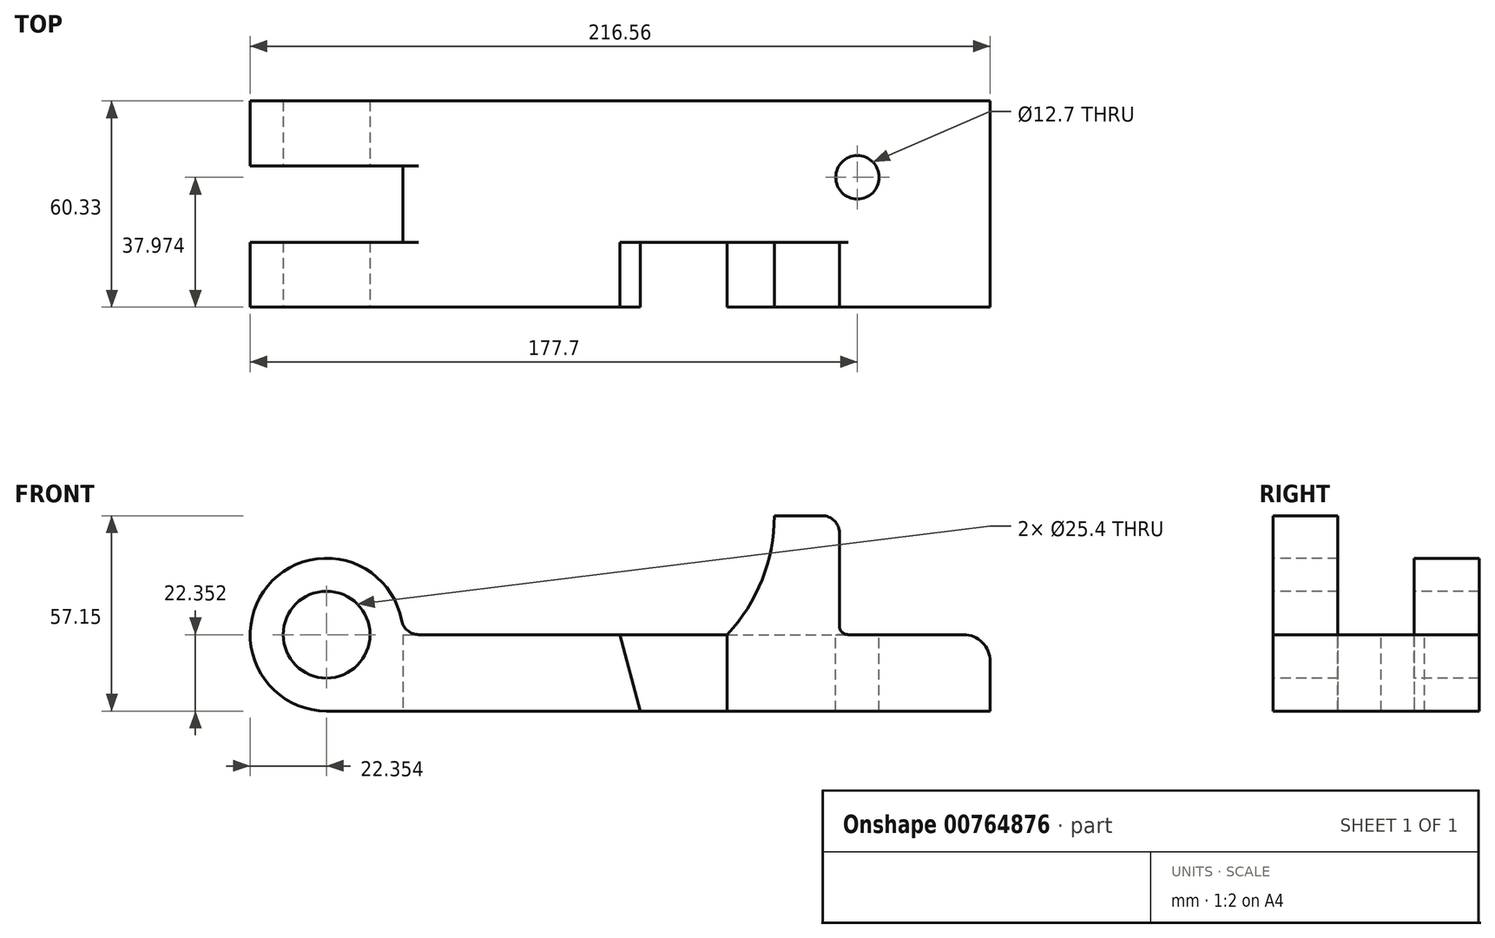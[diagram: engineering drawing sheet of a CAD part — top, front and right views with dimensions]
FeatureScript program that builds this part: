
annotation { "Feature Type Name" : "Feature", "Feature Type Description" : "" }
export const myFeature = defineFeature(function(context is Context, id is Id, definition is map)
    precondition{}
    {
        {
            var Q0;
            Q0=qCreatedBy(makeId("Front.planeOp"),FACE);
            var sketch = newSketch(context, id + "F0", { "sketchPlane" : qUnion([Q0])});
            skLineSegment(sketch, "E0", {"start": v(-51.89, 0) * mm, "end": v(142.32, 0) * mm});
            skLineSegment(sketch, "E1", {"start": v(142.32, 0) * mm, "end": v(142.32, 22.35) * mm});
            skLineSegment(sketch, "E2", {"start": v(-51.89, 0) * mm, "end": v(-51.89, 22.35) * mm});
            skCircle(sketch, "E3", {"center": v(-51.89, 22.35) * mm, "radius": 22.35 * mm});
            skCircle(sketch, "E4", {"center": v(-51.89, 22.35) * mm, "radius": 12.7 * mm});
            skLineSegment(sketch, "E5", {"start": v(-51.89, 22.35) * mm, "end": v(142.32, 22.35) * mm});
            skSolve(sketch);
        }
        {
            var Q0;
            {var subQ0=sQuery(id+"F0.wireOp",EDGE,"E0");Q0=makeQuery(id+"F0.imprint","IMPRINT",FACE,{"disambiguationData":[TD([[makeQuery(id+"F0.imprint","IMPRINT",EDGE,{"derivedFrom":subQ0}),1.0]])]});}
            var Q1;
            {var subQ1=sQuery(id+"F0.wireOp",EDGE,"E2");var subQ3=sQuery(id+"F0.wireOp",EDGE,"E4");var subQ4=makeQuery(id+"F0.imprint","INTERSECT",VERTEX,{"derivedFrom":[subQ1,subQ3]});Q1=makeQuery(id+"F0.imprint","IMPRINT",FACE,{"disambiguationData":[TD([[makeQuery(id+"F0.imprint","IMPRINT",EDGE,{"disambiguationData":[TD([[subQ4,1.0]])],"derivedFrom":subQ3}),-1.0]])]});}
            var Q2;
            {var subQ1=sQuery(id+"F0.wireOp",EDGE,"E2");var subQ3=sQuery(id+"F0.wireOp",EDGE,"E4");var subQ4=makeQuery(id+"F0.imprint","INTERSECT",VERTEX,{"derivedFrom":[subQ1,subQ3]});Q2=makeQuery(id+"F0.imprint","IMPRINT",FACE,{"disambiguationData":[TD([[makeQuery(id+"F0.imprint","IMPRINT",EDGE,{"disambiguationData":[TD([[subQ4,-1.0]])],"derivedFrom":subQ3}),-1.0]])]});}
            extrude(context, id + "F1", {"entities" : qUnion([Q0, Q1, Q2]), "oppositeDirection" : true, "depth" : 41.33 * mm, "offsetDistance" : 25.4 * mm});
        }
        {
            var Q0;
            Q0=makeQuery(id+"F1.opExtrude","CAP_FACE",FACE,{"disambiguationData":[OSD([sQuery(id+"F0.wireOp",EDGE,"E0"),sQuery(id+"F0.wireOp",EDGE,"E1"),sQuery(id+"F0.wireOp",EDGE,"E3"),sQuery(id+"F0.wireOp",EDGE,"E4"),sQuery(id+"F0.wireOp",EDGE,"E5")])],"isStart":true});
            var sketch = newSketch(context, id + "F2", { "sketchPlane" : qUnion([Q0])});
            skCircle(sketch, "E6", {"center": v(-51.89, 22.35) * mm, "radius": 12.7 * mm});
            skCircle(sketch, "E7", {"center": v(-51.89, 22.35) * mm, "radius": 22.35 * mm});
            skLineSegment(sketch, "E8", {"start": v(-29.53, 22.35) * mm, "end": v(142.32, 22.35) * mm});
            skLineSegment(sketch, "E9", {"start": v(142.32, 22.35) * mm, "end": v(142.32, 0) * mm});
            skLineSegment(sketch, "E10", {"start": v(142.32, 0) * mm, "end": v(-51.89, 0) * mm});
            skLineSegment(sketch, "E11", {"start": v(33.97, 22.35) * mm, "end": v(39.96, 0) * mm});
            skLineSegment(sketch, "E12", {"start": v(65.36, 0) * mm, "end": v(65.36, 22.35) * mm});
            skLineSegment(sketch, "E13", {"start": v(98.2, 0) * mm, "end": v(98.2, 57.15) * mm});
            skCircle(sketch, "E14", {"center": v(28.35, 57.15) * mm, "radius": 50.8 * mm});
            skLineSegment(sketch, "E15", {"start": v(98.2, 57.15) * mm, "end": v(79.15, 57.15) * mm});
            skSolve(sketch);
        }
        {
            var Q0;
            Q0=makeQuery(id+"F2.imprint","IMPRINT",FACE,{"disambiguationData":[TD([[makeQuery(id+"F2.imprint","IMPRINT",EDGE,{"derivedFrom":sQuery(id+"F2.wireOp",EDGE,"E6")}),-1.0]])]});
            var Q1;
            {var subQ1=sQuery(id+"F2.wireOp",EDGE,"E10");var subQ5=sQuery(id+"F2.wireOp",EDGE,"E7");var subQ6=makeQuery(id+"F2.imprint","INTERSECT",VERTEX,{"derivedFrom":[subQ5,subQ1]});Q1=makeQuery(id+"F2.imprint","IMPRINT",FACE,{"disambiguationData":[TD([[makeQuery(id+"F2.imprint","IMPRINT",EDGE,{"disambiguationData":[TD([[subQ6,-1.0]])],"derivedFrom":subQ5}),-1.0]])]});}
            var Q2;
            {var subQ0=sQuery(id+"F2.wireOp",EDGE,"E11");var subQ1=sQuery(id+"F2.wireOp",EDGE,"E8");var subQ2=makeQuery(id+"F2.imprint","INTERSECT",VERTEX,{"derivedFrom":[subQ1,subQ0]});Q2=makeQuery(id+"F2.imprint","IMPRINT",FACE,{"disambiguationData":[TD([[makeQuery(id+"F2.imprint","IMPRINT",EDGE,{"disambiguationData":[TD([[subQ2,1.0]])],"derivedFrom":subQ1}),-1.0]])]});}
            var Q3;
            {var subQ0=sQuery(id+"F2.wireOp",EDGE,"E13");var subQ3=sQuery(id+"F2.wireOp",EDGE,"E8");var subQ4=makeQuery(id+"F2.imprint","INTERSECT",VERTEX,{"derivedFrom":[subQ3,subQ0]});Q3=makeQuery(id+"F2.imprint","IMPRINT",FACE,{"disambiguationData":[TD([[makeQuery(id+"F2.imprint","IMPRINT",EDGE,{"disambiguationData":[TD([[subQ4,1.0]])],"derivedFrom":subQ3}),-1.0]])]});}
            var Q4;
            {var subQ5=sQuery(id+"F2.wireOp",EDGE,"E15");Q4=makeQuery(id+"F2.imprint","IMPRINT",FACE,{"disambiguationData":[TD([[makeQuery(id+"F2.imprint","IMPRINT",EDGE,{"derivedFrom":subQ5}),1.0]])]});}
            var Q5;
            {var subQ0=sQuery(id+"F2.wireOp",EDGE,"E9");Q5=makeQuery(id+"F2.imprint","IMPRINT",FACE,{"disambiguationData":[TD([[makeQuery(id+"F2.imprint","IMPRINT",EDGE,{"derivedFrom":subQ0}),1.0]])]});}
            extrude(context, id + "F3", {"entities" : qUnion([Q0, Q1, Q2, Q3, Q4, Q5]), "operationType" : NewBodyOperationType.ADD, "depth" : 19 * mm, "offsetDistance" : 25.4 * mm});
        }
        {
            var Q0;
            Q0=makeQuery(id+"F3.opExtrude","SWEPT_EDGE",EDGE,{"disambiguationData":[OSD([sQuery(id+"F2.wireOp",EDGE,"E13"),sQuery(id+"F2.wireOp",EDGE,"E15")])]});
            fillet(context, id + "F4", {"entities" : qUnion([Q0]), "radius" : 5.08 * mm, "tangentPropagation" : true, "allowEdgeOverflow" : false});
        }
        {
            var Q0;
            {var subQ0=sQuery(id+"F2.wireOp",EDGE,"E8");Q0=makeQuery(id+"F3.boolean.opBoolean","MERGE",FACE,{"derivedFrom":[makeQuery(id+"F1.opExtrude","SWEPT_FACE",FACE,{"disambiguationData":[OSD([sQuery(id+"F0.wireOp",EDGE,"E5")])]}),makeQuery(id+"F3.opExtrude","SWEPT_FACE",FACE,{"disambiguationData":[OSD([subQ0]),TDD([makeQuery(id+"F2.imprint","IMPRINT",EDGE,{"disambiguationData":[TD([[makeQuery(id+"F2.imprint","INTERSECT",VERTEX,{"derivedFrom":[sQuery(id+"F2.wireOp",EDGE,"E7"),subQ0]}),-1.0]])],"derivedFrom":subQ0}),makeQuery(id+"F2.imprint","IMPRINT",EDGE,{"disambiguationData":[TD([[makeQuery(id+"F2.imprint","INTERSECT",VERTEX,{"derivedFrom":[subQ0,sQuery(id+"F2.wireOp",EDGE,"E11")]}),1.0]])],"derivedFrom":subQ0})])]}),makeQuery(id+"F3.opExtrude","SWEPT_FACE",FACE,{"disambiguationData":[OSD([subQ0]),TDD([makeQuery(id+"F2.imprint","IMPRINT",EDGE,{"disambiguationData":[TD([[makeQuery(id+"F2.imprint","INTERSECT",VERTEX,{"derivedFrom":[subQ0,sQuery(id+"F2.wireOp",EDGE,"E9")]}),1.0]])],"derivedFrom":subQ0})])]})]});}
            var sketch = newSketch(context, id + "F5", { "sketchPlane" : qUnion([Q0])});
            skLineSegment(sketch, "E16", {"start": v(142.32, 41.33) * mm, "end": v(103.46, 41.33) * mm});
            skLineSegment(sketch, "E17", {"start": v(103.46, 41.33) * mm, "end": v(103.46, 18.97) * mm});
            skPoint(sketch, "E18", {"position": v(103.46, 18.97) * mm});
            skSolve(sketch);
        }
        {
            var Q0;
            Q0=sQuery(id+"F5.wireOp",VERTEX,"E18");
            var Q1;
            Q1=makeQuery(id+"F1.opExtrude","SWEPT_BODY",BODY,{"disambiguationData":[OSD([sQuery(id+"F0.wireOp",EDGE,"E0"),sQuery(id+"F0.wireOp",EDGE,"E1"),sQuery(id+"F0.wireOp",EDGE,"E3"),sQuery(id+"F0.wireOp",EDGE,"E4"),sQuery(id+"F0.wireOp",EDGE,"E5")])]});
            hole(context, id + "F6", {"style" : HoleStyle.SIMPLE, "endStyle" : HoleEndStyle.THROUGH, "holeDiameter" : 12.7 * mm, "majorDiameter" : 6.35 * mm, "isTappedThrough" : true, "tappedDepth" : 12.7 * mm, "tapClearance" : 3, "locations" : qUnion([Q0]), "scope" : qUnion([Q1])});
        }
        {
            var Q0;
            Q0=makeQuery(id+"F3.boolean.opBoolean","MERGE",EDGE,{"derivedFrom":[makeQuery(id+"F1.opExtrude","SWEPT_EDGE",EDGE,{"disambiguationData":[OSD([sQuery(id+"F0.wireOp",EDGE,"E1"),sQuery(id+"F0.wireOp",EDGE,"E5")])]}),makeQuery(id+"F3.opExtrude","SWEPT_EDGE",EDGE,{"disambiguationData":[OSD([sQuery(id+"F2.wireOp",EDGE,"E8"),sQuery(id+"F2.wireOp",EDGE,"E9")])]})]});
            fillet(context, id + "F7", {"entities" : qUnion([Q0]), "radius" : 7.87 * mm, "tangentPropagation" : true, "allowEdgeOverflow" : false});
        }
        {
            var Q0;
            Q0=makeQuery(id+"F3.opExtrude","SWEPT_EDGE",EDGE,{"disambiguationData":[OSD([sQuery(id+"F2.wireOp",EDGE,"E8"),sQuery(id+"F2.wireOp",EDGE,"E13")])]});
            fillet(context, id + "F8", {"entities" : qUnion([Q0]), "radius" : 2.54 * mm, "tangentPropagation" : true, "allowEdgeOverflow" : false});
        }
        {
            var Q0;
            {var subQ0=sQuery(id+"F2.wireOp",EDGE,"E8");Q0=makeQuery(id+"F3.boolean.opBoolean","MERGE",FACE,{"derivedFrom":[makeQuery(id+"F1.opExtrude","SWEPT_FACE",FACE,{"disambiguationData":[OSD([sQuery(id+"F0.wireOp",EDGE,"E5")])]}),makeQuery(id+"F3.opExtrude","SWEPT_FACE",FACE,{"disambiguationData":[OSD([subQ0]),TDD([makeQuery(id+"F2.imprint","IMPRINT",EDGE,{"disambiguationData":[TD([[makeQuery(id+"F2.imprint","INTERSECT",VERTEX,{"derivedFrom":[sQuery(id+"F2.wireOp",EDGE,"E7"),subQ0]}),-1.0]])],"derivedFrom":subQ0}),makeQuery(id+"F2.imprint","IMPRINT",EDGE,{"disambiguationData":[TD([[makeQuery(id+"F2.imprint","INTERSECT",VERTEX,{"derivedFrom":[subQ0,sQuery(id+"F2.wireOp",EDGE,"E11")]}),1.0]])],"derivedFrom":subQ0})])]}),makeQuery(id+"F3.opExtrude","SWEPT_FACE",FACE,{"disambiguationData":[OSD([subQ0]),TDD([makeQuery(id+"F2.imprint","IMPRINT",EDGE,{"disambiguationData":[TD([[makeQuery(id+"F2.imprint","INTERSECT",VERTEX,{"derivedFrom":[subQ0,sQuery(id+"F2.wireOp",EDGE,"E9")]}),1.0]])],"derivedFrom":subQ0})])]})]});}
            var sketch = newSketch(context, id + "F9", { "sketchPlane" : qUnion([Q0])});
            skLineSegment(sketch, "E19", {"start": v(-29.53, 41.33) * mm, "end": v(-29.53, 22.33) * mm});
            skLineSegment(sketch, "E20", {"start": v(-29.53, 22.33) * mm, "end": v(-83.2, 22.33) * mm});
            skLineSegment(sketch, "E21", {"start": v(-29.53, -19) * mm, "end": v(-29.53, 0) * mm});
            skLineSegment(sketch, "E22", {"start": v(-29.53, 0) * mm, "end": v(-83.2, 0) * mm});
            skLineSegment(sketch, "E23", {"start": v(-83.2, 0) * mm, "end": v(-83.2, 22.33) * mm});
            skLineSegment(sketch, "E24", {"start": v(-29.53, 22.33) * mm, "end": v(-29.53, 0) * mm});
            skSolve(sketch);
        }
        {
            var Q0;
            Q0=makeQuery(id+"F9.imprint","IMPRINT",FACE,{"disambiguationData":[TD([[makeQuery(id+"F9.imprint","IMPRINT",EDGE,{"derivedFrom":sQuery(id+"F9.wireOp",EDGE,"E20")}),1.0]])]});
            extrude(context, id + "F10", {"entities" : qUnion([Q0]), "operationType" : NewBodyOperationType.REMOVE, "depth" : 127 * mm, "offsetDistance" : 25.4 * mm, "symmetric" : true});
        }
        {
            var Q0;
            {var subQ0=sQuery(id+"F2.wireOp",EDGE,"E11");var subQ1=sQuery(id+"F2.wireOp",EDGE,"E8");var subQ2=sQuery(id+"F2.wireOp",EDGE,"E7");var subQ3=makeQuery(id+"F3.opExtrude","SWEPT_FACE",FACE,{"disambiguationData":[OSD([subQ2])]});var subQ4=sQuery(id+"F0.wireOp",EDGE,"E3");var subQ5=makeQuery(id+"F1.opExtrude","SWEPT_FACE",FACE,{"disambiguationData":[OSD([subQ4])]});var subQ6=sQuery(id+"F0.wireOp",EDGE,"E5");var subQ7=makeQuery(id+"F1.opExtrude","SWEPT_FACE",FACE,{"disambiguationData":[OSD([subQ6])]});var subQ8=makeQuery(id+"F3.opExtrude","SWEPT_FACE",FACE,{"disambiguationData":[OSD([subQ1]),TDD([makeQuery(id+"F2.imprint","IMPRINT",EDGE,{"disambiguationData":[TD([[makeQuery(id+"F2.imprint","INTERSECT",VERTEX,{"derivedFrom":[subQ1,sQuery(id+"F2.wireOp",EDGE,"E9")]}),1.0]])],"derivedFrom":subQ1})])]});var subQ10=makeQuery(id+"F3.opExtrude","SWEPT_FACE",FACE,{"disambiguationData":[OSD([subQ1]),TDD([makeQuery(id+"F2.imprint","IMPRINT",EDGE,{"disambiguationData":[TD([[makeQuery(id+"F2.imprint","INTERSECT",VERTEX,{"derivedFrom":[subQ2,subQ1]}),-1.0]])],"derivedFrom":subQ1}),makeQuery(id+"F2.imprint","IMPRINT",EDGE,{"disambiguationData":[TD([[makeQuery(id+"F2.imprint","INTERSECT",VERTEX,{"derivedFrom":[subQ1,subQ0]}),1.0]])],"derivedFrom":subQ1})])]});Q0=makeQuery(id+"F10.boolean.opBoolean","SPLIT",EDGE,{"disambiguationData":[topologyDisambiguationEdgeConnected([subQ5,subQ7,subQ3,subQ10,subQ8]),TD([makeQuery(id+"F10.opExtrude","SWEPT_FACE",FACE,{"disambiguationData":[OSD([sQuery(id+"F9.wireOp",EDGE,"E22")])]})])],"derivedFrom":makeQuery(id+"F3.boolean.opBoolean","MERGE",EDGE,{"derivedFrom":[makeQuery(id+"F1.opExtrude","SWEPT_EDGE",EDGE,{"disambiguationData":[OSD([subQ4,subQ6])]}),makeQuery(id+"F3.opExtrude","SWEPT_EDGE",EDGE,{"disambiguationData":[OSD([subQ2,subQ1])]})]})});}
            var Q1;
            {var subQ0=sQuery(id+"F2.wireOp",EDGE,"E7");var subQ1=makeQuery(id+"F3.opExtrude","SWEPT_FACE",FACE,{"disambiguationData":[OSD([subQ0])]});var subQ2=sQuery(id+"F0.wireOp",EDGE,"E3");var subQ3=makeQuery(id+"F1.opExtrude","SWEPT_FACE",FACE,{"disambiguationData":[OSD([subQ2])]});var subQ4=sQuery(id+"F0.wireOp",EDGE,"E5");var subQ5=makeQuery(id+"F1.opExtrude","SWEPT_FACE",FACE,{"disambiguationData":[OSD([subQ4])]});var subQ6=sQuery(id+"F2.wireOp",EDGE,"E8");var subQ7=makeQuery(id+"F3.opExtrude","SWEPT_FACE",FACE,{"disambiguationData":[OSD([subQ6]),TDD([makeQuery(id+"F2.imprint","IMPRINT",EDGE,{"disambiguationData":[TD([[makeQuery(id+"F2.imprint","INTERSECT",VERTEX,{"derivedFrom":[subQ6,sQuery(id+"F2.wireOp",EDGE,"E9")]}),1.0]])],"derivedFrom":subQ6})])]});var subQ9=makeQuery(id+"F3.opExtrude","SWEPT_FACE",FACE,{"disambiguationData":[OSD([subQ6]),TDD([makeQuery(id+"F2.imprint","IMPRINT",EDGE,{"disambiguationData":[TD([[makeQuery(id+"F2.imprint","INTERSECT",VERTEX,{"derivedFrom":[subQ0,subQ6]}),-1.0]])],"derivedFrom":subQ6}),makeQuery(id+"F2.imprint","IMPRINT",EDGE,{"disambiguationData":[TD([[makeQuery(id+"F2.imprint","INTERSECT",VERTEX,{"derivedFrom":[subQ6,sQuery(id+"F2.wireOp",EDGE,"E11")]}),1.0]])],"derivedFrom":subQ6})])]});Q1=makeQuery(id+"F10.boolean.opBoolean","SPLIT",EDGE,{"disambiguationData":[topologyDisambiguationEdgeConnected([subQ3,subQ5,subQ1,subQ9,subQ7]),TD([makeQuery(id+"F10.opExtrude","SWEPT_FACE",FACE,{"disambiguationData":[OSD([sQuery(id+"F9.wireOp",EDGE,"E20")])]})])],"derivedFrom":makeQuery(id+"F3.boolean.opBoolean","MERGE",EDGE,{"derivedFrom":[makeQuery(id+"F1.opExtrude","SWEPT_EDGE",EDGE,{"disambiguationData":[OSD([subQ2,subQ4])]}),makeQuery(id+"F3.opExtrude","SWEPT_EDGE",EDGE,{"disambiguationData":[OSD([subQ0,subQ6])]})]})});}
            fillet(context, id + "F11", {"entities" : qUnion([Q0, Q1]), "radius" : 5.08 * mm, "tangentPropagation" : true, "allowEdgeOverflow" : false});
        }
    });
